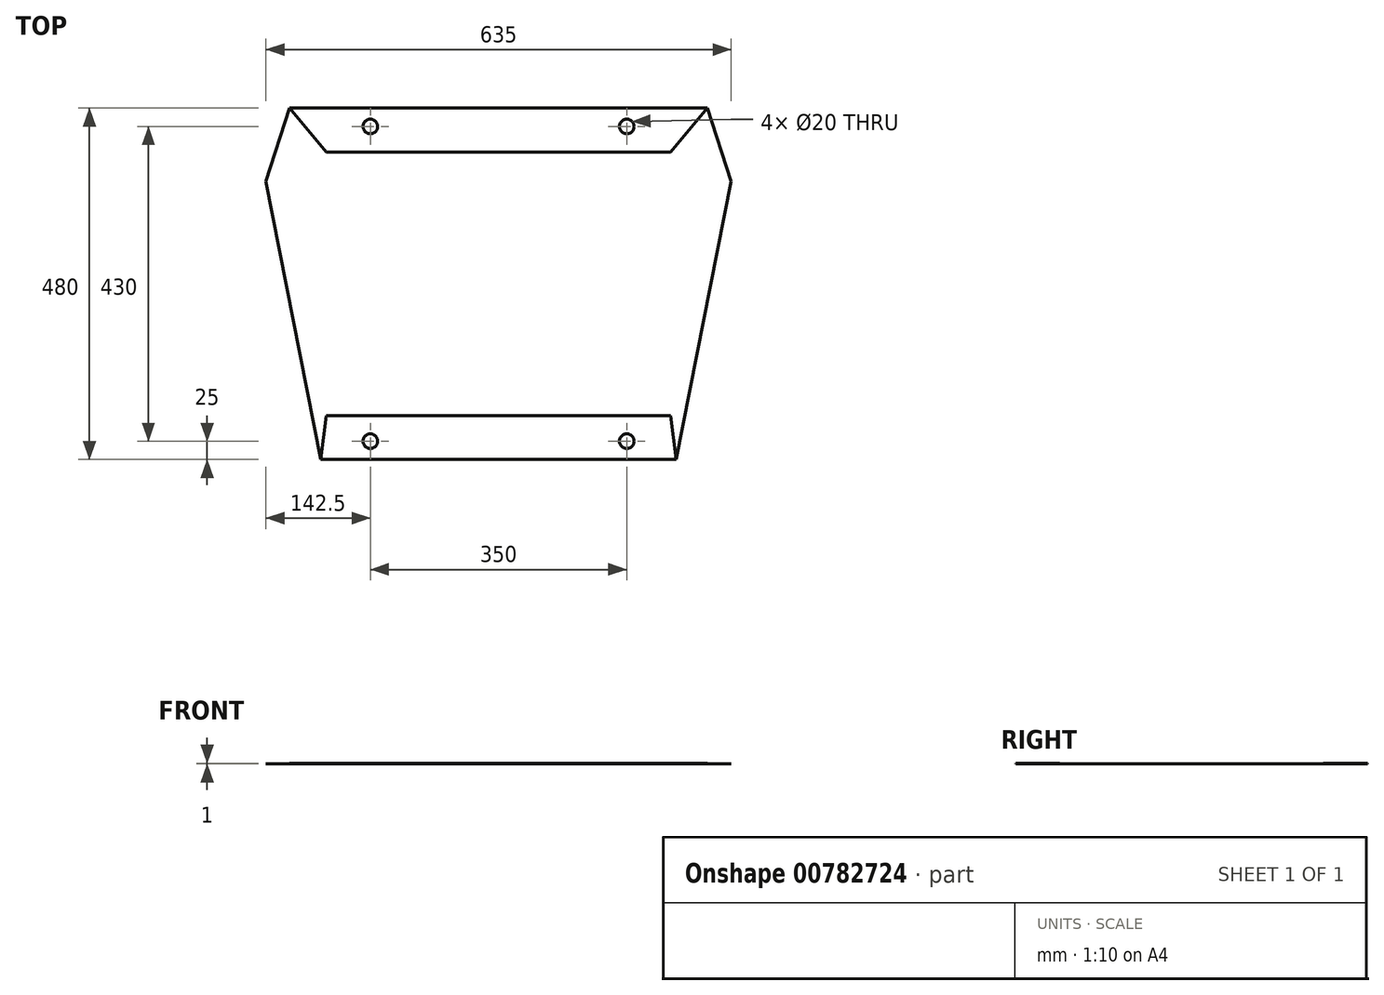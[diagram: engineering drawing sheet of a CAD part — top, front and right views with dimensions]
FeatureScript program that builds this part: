
annotation { "Feature Type Name" : "Feature", "Feature Type Description" : "" }
export const myFeature = defineFeature(function(context is Context, id is Id, definition is map)
    precondition{}
    {
        {
            var Q0;
            Q0=qCreatedBy(makeId("Top.planeOp"),FACE);
            var sketch = newSketch(context, id + "F0", { "sketchPlane" : qUnion([Q0])});
            skLineSegment(sketch, "E0", {"start": v(-570, 0) * mm, "end": v(0, 0) * mm});
            skLineSegment(sketch, "E1", {"start": v(0, 0) * mm, "end": v(32.5, -100) * mm});
            skLineSegment(sketch, "E2", {"start": v(32.5, -100) * mm, "end": v(-42.5, -480) * mm});
            skLineSegment(sketch, "E3", {"start": v(-42.5, -480) * mm, "end": v(-527.5, -480) * mm});
            skLineSegment(sketch, "E4", {"start": v(-527.5, -480) * mm, "end": v(-602.5, -100) * mm});
            skLineSegment(sketch, "E5", {"start": v(-602.5, -100) * mm, "end": v(-570, 0) * mm});
            skSolve(sketch);
        }
        {
            var Q0;
            Q0=qSketchRegion(id+"F0",true);
            extrude(context, id + "F1", {"entities" : qUnion([Q0]), "depth" : .5 * mm, "offsetDistance" : 25 * mm});
        }
        {
            var Q0;
            Q0=makeQuery(id+"F1.opExtrude","CAP_FACE",FACE,{"disambiguationData":[OSD([sQuery(id+"F0.wireOp",EDGE,"E0"),sQuery(id+"F0.wireOp",EDGE,"E1"),sQuery(id+"F0.wireOp",EDGE,"E2"),sQuery(id+"F0.wireOp",EDGE,"E3"),sQuery(id+"F0.wireOp",EDGE,"E4"),sQuery(id+"F0.wireOp",EDGE,"E5")])],"isStart":false});
            var sketch = newSketch(context, id + "F2", { "sketchPlane" : qUnion([Q0])});
            skLineSegment(sketch, "E6", {"start": v(-570, 0) * mm, "end": v(-520, -60) * mm});
            skLineSegment(sketch, "E7", {"start": v(-520, -60) * mm, "end": v(-50, -60) * mm});
            skLineSegment(sketch, "E8", {"start": v(-50, -60) * mm, "end": v(0, 0) * mm});
            skLineSegment(sketch, "E9", {"start": v(0, 0) * mm, "end": v(-570, 0) * mm});
            skLineSegment(sketch, "E10.0", {"start": v(-42.5, -480) * mm, "end": v(-527.5, -480) * mm});
            skLineSegment(sketch, "E11", {"start": v(-527.5, -480) * mm, "end": v(-520, -420) * mm});
            skLineSegment(sketch, "E12", {"start": v(-520, -420) * mm, "end": v(-50, -420) * mm});
            skLineSegment(sketch, "E13", {"start": v(-50, -420) * mm, "end": v(-42.5, -480) * mm});
            skSolve(sketch);
        }
        {
            var Q0;
            Q0=qSketchRegion(id+"F2",true);
            extrude(context, id + "F3", {"entities" : qUnion([Q0]), "operationType" : NewBodyOperationType.ADD, "depth" : .5 * mm, "offsetDistance" : 25 * mm});
        }
        {
            var Q0;
            Q0=makeQuery(id+"F3.opExtrude","CAP_FACE",FACE,{"disambiguationData":[OSD([sQuery(id+"F2.wireOp",EDGE,"E6"),sQuery(id+"F2.wireOp",EDGE,"E7"),sQuery(id+"F2.wireOp",EDGE,"E8"),sQuery(id+"F2.wireOp",EDGE,"E9")])],"isStart":false});
            var sketch = newSketch(context, id + "F4", { "sketchPlane" : qUnion([Q0])});
            skCircle(sketch, "E14", {"center": v(-460, -25) * mm, "radius": 10 * mm});
            skCircle(sketch, "E15.0.1.0", {"center": v(-460, -455) * mm, "radius": 10 * mm});
            skCircle(sketch, "E15.1.0.0", {"center": v(-110, -25) * mm, "radius": 10 * mm});
            skCircle(sketch, "E15.1.1.0", {"center": v(-110, -455) * mm, "radius": 10 * mm});
            skLineSegment(sketch, "E15.direction1", {"start": v(-460, -25) * mm, "end": v(-110, -25) * mm, "construction": true});
            skLineSegment(sketch, "E15.direction2", {"start": v(-460, -25) * mm, "end": v(-460, -455) * mm, "construction": true});
            skSolve(sketch);
        }
        {
            var Q0;
            Q0 = qSketchRegion(id + "F4", true);
            extrude(context, id + "F5", {"entities" : qUnion([Q0]), "operationType" : NewBodyOperationType.REMOVE, "endBound" : BoundingType.THROUGH_ALL, "oppositeDirection" : true, "depth" : 25 * mm, "offsetDistance" : 25 * mm});
        }
    });
